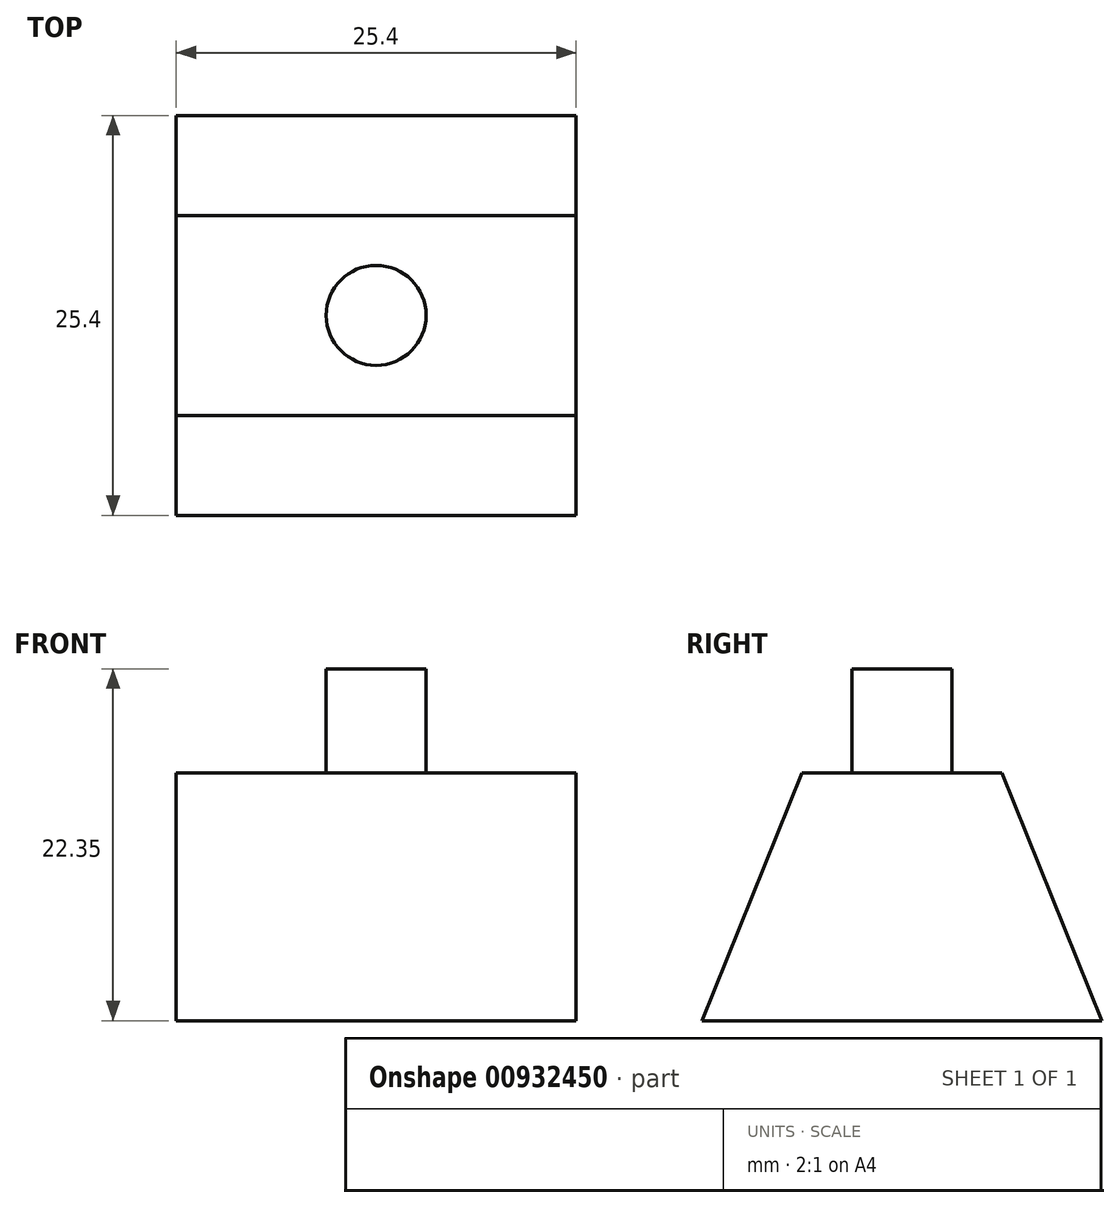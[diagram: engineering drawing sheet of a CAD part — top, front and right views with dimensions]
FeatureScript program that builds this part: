
annotation { "Feature Type Name" : "Feature", "Feature Type Description" : "" }
export const myFeature = defineFeature(function(context is Context, id is Id, definition is map)
    precondition{}
    {
        {
            var Q0;
            Q0=qCreatedBy(makeId("Right.planeOp"),FACE);
            var sketch = newSketch(context, id + "F0", { "sketchPlane" : qUnion([Q0])});
            skLineSegment(sketch, "E0", {"start": v(-12.7, 0) * mm, "end": v(12.7, 0) * mm});
            skLineSegment(sketch, "E1", {"start": v(12.7, 0) * mm, "end": v(6.35, 15.75) * mm});
            skLineSegment(sketch, "E2", {"start": v(6.35, 15.75) * mm, "end": v(-6.35, 15.75) * mm});
            skLineSegment(sketch, "E3", {"start": v(-6.35, 15.75) * mm, "end": v(-12.7, 0) * mm});
            skLineSegment(sketch, "E4", {"start": v(0, 0) * mm, "end": v(0, 15.75) * mm, "construction": true});
            skSolve(sketch);
        }
        {
            var Q0;
            Q0 = qSketchRegion(id + "F0", true);
            extrude(context, id + "F1", {"entities" : qUnion([Q0]), "depth" : 25.4 * mm, "offsetDistance" : 25.4 * mm});
        }
        {
            var Q0;
            Q0=makeQuery(id+"F1.opExtrude","SWEPT_FACE",FACE,{"disambiguationData":[OSD([sQuery(id+"F0.wireOp",EDGE,"E2")])]});
            var sketch = newSketch(context, id + "F2", { "sketchPlane" : qUnion([Q0])});
            skLineSegment(sketch, "E5", {"start": v(0, 0) * mm, "end": v(25.4, 0) * mm, "construction": true});
            skCircle(sketch, "E6", {"center": v(12.7, 0) * mm, "radius": 3.18 * mm});
            skSolve(sketch);
        }
        {
            var Q0;
            Q0 = qSketchRegion(id + "F2", true);
            extrude(context, id + "F3", {"entities" : qUnion([Q0]), "operationType" : NewBodyOperationType.ADD, "depth" : 6.6 * mm, "offsetDistance" : 25.4 * mm});
        }
    });
